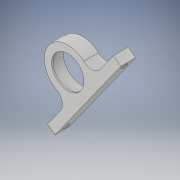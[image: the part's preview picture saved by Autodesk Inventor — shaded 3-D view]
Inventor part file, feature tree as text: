
AUTODESK INVENTOR PART (.ipt)
format: ipt  version: 2017 (Build 210142000, 142)  size: 145,408 bytes
history: native  units: in
note: dims shown in document units (in); Inventor stores cm internally (conversion verified against a paired STEP export)
features: other x4, extrude x3, sketch x3, reference x3, projected_geometry x2
ambient origin geometry x8: Origin, YZ Plane, XZ Plane, XY Plane, X Axis, Y Axis, Z Axis, Center Point
bodies: Solid1 (feature_tree)
feature tree (15):
  extrude  "Extrusion1"  Depth=0.3346in TaperAngle=0.0deg
  extrude  "Extrusion2"  Depth=0.0315in TaperAngle=0.0deg
  extrude  "Extrusion3"  Depth=2.5591in
  sketch  "Sketch1"  dims[d0=0.0984in d1=0.3346in d2=0.0in]
  reference  "Reference1"
  reference  "Reference2"
  sketch  "Sketch2"  dims[d3=0.7309in d4=0.0315in d5=0.0in]
  reference  "Reference3"
  sketch  "Sketch3"  dims[d8=0.0591in d9=0.0in d10=0.1378in d11=0.1378in d12=2.5591in d13=0.1575in d14=0.1575in d15=0.8858in]
  projected_geometry  "Projected Loop1"
  projected_geometry  "Projected Loop2"
  other  "Rubiks Arm Assembly.iam"
  other  "8mmx22mm bearing:1"
  other  "Base Plate:1"
  other  "coupler:1"
